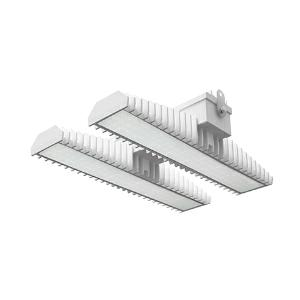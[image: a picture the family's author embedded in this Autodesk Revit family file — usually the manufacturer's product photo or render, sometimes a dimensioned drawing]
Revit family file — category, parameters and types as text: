
# Revit family: 3f_filippi_-_3f_lem_ho_concentrato_3f_filippi_-_58978_a0812_-_3f_lem_2_ho_led_140_dali_cr_conc___vs_605e
name_source: partatom
category: Lighting Fixtures
units: mm (PartAtom-declared; Revit-internal decimal feet)

## family parameters
Cut with Voids When Loaded = No
Host = Face
Light Source = No
Part Type = Normal
Room Calculation Point = No
Round Connector Dimension = Use Diameter
Shared = No

## types (1)
- 3F Filippi - 3F LEM HO Concentrato (1 x LED, 17583 lm, 138 W, 4000 K)
    Apparent Load = 138 VA
    Approval mark = CE
    CIE Flux Codes = 78 93 98 100 100
    Color Rendering = 80
    Color Temperature = 4000 K
    Control Gear = Electronic transformer
    Default Elevation = 1800 mm
    Description = Industrial luminaire with high light output and high luminous efficiency designed with the most innovative technologies for environments with temperature up to 55°C.

ILLUMINOTECHNICAL
Luminous efficiency 100% (DLOR 98%, ULOR 2%).
Initial luminous flux of the luminaire 17583 lm.
Direct symmetric narrow distribution: the illuminated area has a elliptical shape.
Installation Interdistance Transv.D = 0.60 x hu - Long.D = 0.91 x hu.
Tabular UGR (CIE 117 - 4H-8H; S=0.25H; 70/50/20): RUG 20.5 - 22.
Beam angle: 38° - 61°.
Luminous efficacy 127 lm/W.
Lifetime (L93/B10): 30000 h. (tq+25°C)
Lifetime (L90/B10): 50000 h. (tq+25°C)
Lifetime (L85/B10): 80000 h. (tq+25°C)
Lifetime (L80/B10): 100000 h. (tq+25°C)
Lifetime (L85/B10): 50000 h. (tq+55°C)
Sudden decreased luminous flux after 50000 hours: 0% (C0).
Photobiological safety in compliance with IEC/TR 62778: RG0 risk exempt, (IEC 62471).
In compliance with IEC/EN 62722-2-1 - IEC/EN 62717 standards.

SOURCE
2 Mid-Power linear LED modules 70W/840.
Energy efficiency class (UE 2019/2020 - UE 2019/2015): C.
CIE 13.3 Colour rendering index: CRI >80 (R9 <50%).
IES TM-30 Fidelity Index: Rf = 84 Rg = 95.
CCT nominal colour temperature 4000 K.
Colour initial tolerance (MacAdam): SDCM 3.

MECHANICAL
Passive modular heatsinks in die-casted aluminium, painted in white colour.
To optimize the thermal management of the LED module, the heatsinks are oversized and provided with self-cleaning of cooling fins.
Wiring body in aluminium and galvanised steel anchored solidly to the sinks and thermally separated.
3F Lens lenses with high luminous efficiency, transparent methacrylate (PMMA), fixed to the LED modules.
Fixing brackets in stainless steel.
Luminaire with limited surface temperature. - D - (EN 60598-2-24)
Dimensions: 470x542 mm, height 133 mm. Weight 10.43 kg.
IP65 protection degree.
Mechanical strength to impacts IK06 (1 joule).
Glow-wire test resistance 650°C.

ELECTRICAL
Halogen Free DALI-2 DATI (Parts 251, 252, 253), PUSH-DIM, electronic wiring 230V-50/60Hz, power factor 0.97 at full load, THD <25%, constant output current, class I, 1 driver, 1 DALI addresse.
Power of the luminaire 138 W.
ENEC - CE.
SAFE FLICKER: PstLM=<1 and SVM=<0.4 (IEC TR 61547-1 and IEC TR 63158), to ensure a more comfortable and safe light.
Luminaire compliant with EN 60598-2-22 for power supply from a centralised emergency system CPSS (Central Power Supply System), not incorporated in the luminaire - high risk areas excluded. The default power and flux are 100% in AC and 15% in DC.
Ambient temperature from -30°C to +55°C.
Temperature class T6 max 85°C.
Quick connection via M25 5P connector with 9-13 mm tightening range.
Power unit positioned on a separate compartment by the LED module to ensure optimum temperatures of cabling components, to be inspectable and maintainable.
Relative humidity UR: <85%.

INSTALLATION
Ceiling / Suspended / Wall.
All accessories dedicated to this product are available on the Catalog and on our website www.3F-Filippi.com.

ACCESSORIES
A0812 - Anti-glare microprismatic VS moulded glass, tempered, not flammable, with sealing gasket.
One required for each light module. The pack contains 10 pieces.

APPLICATIONS
In commercial environments, exhibition and industrial areas, stores, open areas or with shelves.
Environments in which it is necessary a total protection against falling fragments (eg environments with foodstuffs or machines with moving parts or with extreme temperature changes), use luminaires with polycarbonate lenses.

LIGHT MANAGEMENT
Recommended minimum setting: 10%.
The luminaire, equipped with (DALI-2 DATI) driver, can be controlled manually with 3F Easy Dim technology or automatically/manually with wired or wireless DALI/D2D control systems.
The D2D driver guarantees interoperability with other devices with the same certification by making the following information available:
Device Data (Part 251), Energy Report (Part 252), Diagnosis & Maintenance (Part 253).
In electrical systems without a regulation system (manual or automatic) and DALI bus, a suitable jumper must be made on the DA-DA terminals of the appliance.

WARNING
Fixture not suitable for cold stores with an ambient temperature <0°C and/or relative humidity >85%.
Luminaire designed for disposal/recycling at end-of-life.
Replaceable (LED only) light source by a professional. Replaceable control gear by a professional.
    Height = 133 mm  [stored 0.436352 ft]
    Lamp = 1 x LED
    Lamp Light Flux = 17583 lm
    Lamp Power = 138 W
    Lamp count = 1
    Length = 470 mm
    Lifetime = 50000 h
    Luminous efficacy = 127 lm/W
    Manufacturer = 3F Filippi
    ModVariant = No
    Model = 3F Filippi - 58978+A0812 - 3F LEM 2 HO LED 140 DALI CR CONC + VS
    Mounting Place = Ceiling
    Mounting Type = Pendant
    Number of Poles = 1
    OnlyDefault = Yes
    Power Factor = 1
    Product Name = 3F Filippi - 3F LEM HO Concentrato
    Product group = pendant luminaire
    ProductGroupID = 9
    Protection Class = Protection class I
    Protection Degree = IP 65
    RLX_Detail_Level = 1
    RLX_Emergency_Light_Flux = 0 lm
    RLX_Emergency_Type = 0
    RLX_Emergency_Type_DB = No
    RlxData = <blob elided: 97897 chars, md5=73b7c02a>
    Socket = socket
    Standby Power = 0 W
    System Light Flux = 17583 lm
    System Power = 138 W
    Type Comments = Product without accessories
    Type Image = 3f_filippi_-_lem_2__a0812.jpg
    URL = http://relux.com
    VarID = ---
    Voltage = 0 V
    Weight = 0.00 kg
    Width = 542 mm

note: [stored X ft] marks values corroborated as IEEE doubles in the binary element streams (Revit-internal decimal feet)

## geometry (parser evidence)
native form markers: Blend x4, Sweep x13
no freeform markers — native parametric forms only
